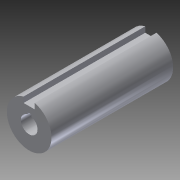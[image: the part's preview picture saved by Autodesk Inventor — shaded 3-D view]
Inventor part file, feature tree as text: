
AUTODESK INVENTOR PART (.ipt)
format: ipt  version: 2013 (Build 170138000, 138)  size: 100,864 bytes
history: native  units: in
note: dims shown in document units (in); Inventor stores cm internally (conversion verified against a paired STEP export)
features: extrude x3, sketch x3
ambient origin geometry x8: Origin, YZ Plane, XZ Plane, XY Plane, X Axis, Y Axis, Z Axis, Center Point
bodies: Solid1 (feature_tree)
feature tree (6):
  extrude  "Extrusion1"  Depth=2.725in TaperAngle=0.0deg
  extrude  "Extrusion2"  Depth=0.125in
  extrude  "Extrusion3"  Depth=0.25in
  sketch  "Sketch1"  dims[d0=1.0in d1=2.725in d2=0.0in]
  sketch  "Sketch2"  dims[d3=2.735in d4=0.0in d5=0.125in]
  sketch  "Sketch3"  dims[d6=0.125in d7=0.25in d8=2.735in d9=0.0in]
